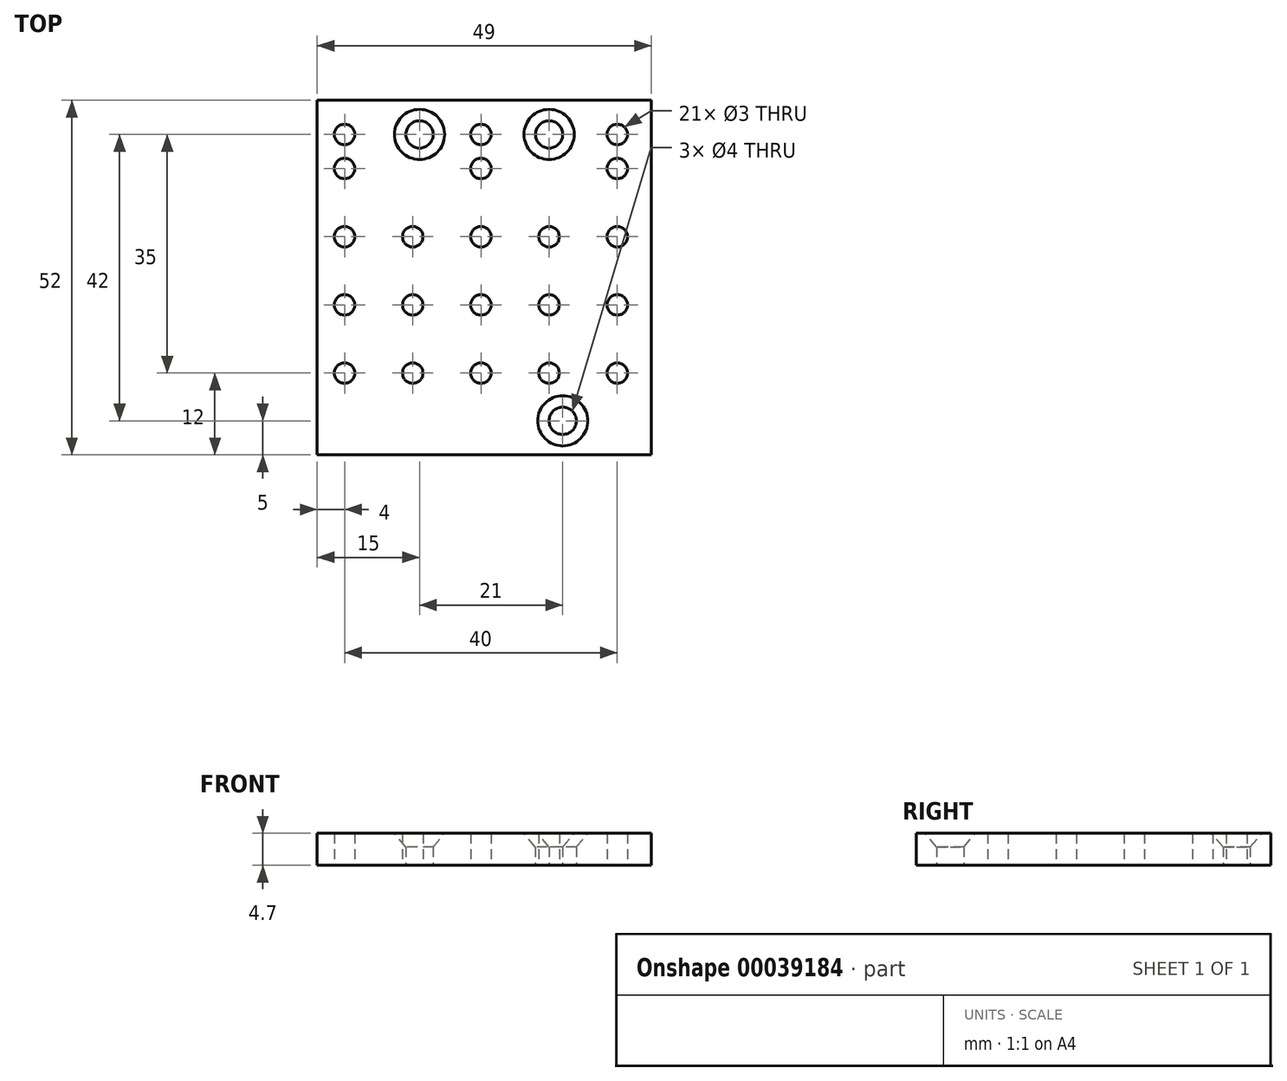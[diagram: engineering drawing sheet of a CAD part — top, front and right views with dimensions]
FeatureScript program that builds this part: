
annotation { "Feature Type Name" : "Feature", "Feature Type Description" : "" }
export const myFeature = defineFeature(function(context is Context, id is Id, definition is map)
    precondition{}
    {
        {
            var Q0;
            Q0=qCreatedBy(makeId("Top.planeOp"),FACE);
            var sketch = newSketch(context, id + "F0", { "sketchPlane" : qUnion([Q0])});
            skLineSegment(sketch, "E0", {"start": v(-52.55, 21) * mm, "end": v(60.16, 21) * mm, "construction": true});
            skLineSegment(sketch, "E1", {"start": v(-53.87, 0) * mm, "end": v(61.05, 0) * mm, "construction": true});
            skLineSegment(sketch, "E2.MirrorCS", {"start": v(-52.55, -21) * mm, "end": v(60.16, -21) * mm, "construction": true});
            skCircle(sketch, "E3", {"center": v(-28.55, 21) * mm, "radius": 2 * mm});
            skCircle(sketch, "E4", {"center": v(-9.55, 21) * mm, "radius": 2 * mm});
            skCircle(sketch, "E5", {"center": v(-7.55, -21) * mm, "radius": 2 * mm});
            skLineSegment(sketch, "E6.bottom", {"start": v(-43.55, 26) * mm, "end": v(5.45, 26) * mm});
            skLineSegment(sketch, "E6.top", {"start": v(-43.55, -26) * mm, "end": v(5.45, -26) * mm});
            skLineSegment(sketch, "E6.left", {"start": v(-43.55, 26) * mm, "end": v(-43.55, -26) * mm});
            skLineSegment(sketch, "E6.right", {"start": v(5.45, 26) * mm, "end": v(5.45, -26) * mm});
            skCircle(sketch, "E7", {"center": v(-28.55, 21) * mm, "radius": 3.5 * mm});
            skCircle(sketch, "E8", {"center": v(-9.55, 21) * mm, "radius": 3.5 * mm});
            skCircle(sketch, "E9", {"center": v(-7.55, -21) * mm, "radius": 3.5 * mm});
            skLineSegment(sketch, "E10", {"start": v(0.45, 28.16) * mm, "end": v(0.45, -29.03) * mm, "construction": true});
            skLineSegment(sketch, "E11", {"start": v(-46.97, 16) * mm, "end": v(10.41, 16) * mm, "construction": true});
            skCircle(sketch, "E12", {"center": v(-39.55, 21) * mm, "radius": 1.5 * mm});
            skCircle(sketch, "E13", {"center": v(-19.55, 21) * mm, "radius": 1.5 * mm});
            skCircle(sketch, "E14", {"center": v(0.45, 21) * mm, "radius": 1.5 * mm});
            skCircle(sketch, "E15", {"center": v(0.45, 16) * mm, "radius": 1.5 * mm});
            skCircle(sketch, "E16.0.1.0", {"center": v(0.45, 6) * mm, "radius": 1.5 * mm});
            skCircle(sketch, "E16.0.2.0", {"center": v(0.45, -4) * mm, "radius": 1.5 * mm});
            skCircle(sketch, "E16.0.3.0", {"center": v(0.45, -14) * mm, "radius": 1.5 * mm});
            skCircle(sketch, "E16.1.1.0", {"center": v(-9.55, 6) * mm, "radius": 1.5 * mm});
            skCircle(sketch, "E16.1.2.0", {"center": v(-9.55, -4) * mm, "radius": 1.5 * mm});
            skCircle(sketch, "E16.1.3.0", {"center": v(-9.55, -14) * mm, "radius": 1.5 * mm});
            skCircle(sketch, "E16.2.0.0", {"center": v(-19.55, 16) * mm, "radius": 1.5 * mm});
            skCircle(sketch, "E16.2.1.0", {"center": v(-19.55, 6) * mm, "radius": 1.5 * mm});
            skCircle(sketch, "E16.2.2.0", {"center": v(-19.55, -4) * mm, "radius": 1.5 * mm});
            skCircle(sketch, "E16.2.3.0", {"center": v(-19.55, -14) * mm, "radius": 1.5 * mm});
            skCircle(sketch, "E16.3.1.0", {"center": v(-29.55, 6) * mm, "radius": 1.5 * mm});
            skCircle(sketch, "E16.3.2.0", {"center": v(-29.55, -4) * mm, "radius": 1.5 * mm});
            skCircle(sketch, "E16.3.3.0", {"center": v(-29.55, -14) * mm, "radius": 1.5 * mm});
            skCircle(sketch, "E16.4.0.0", {"center": v(-39.55, 16) * mm, "radius": 1.5 * mm});
            skCircle(sketch, "E16.4.1.0", {"center": v(-39.55, 6) * mm, "radius": 1.5 * mm});
            skCircle(sketch, "E16.4.2.0", {"center": v(-39.55, -4) * mm, "radius": 1.5 * mm});
            skCircle(sketch, "E16.4.3.0", {"center": v(-39.55, -14) * mm, "radius": 1.5 * mm});
            skLineSegment(sketch, "E16.direction1", {"start": v(0.45, 16) * mm, "end": v(-9.55, 16) * mm, "construction": true});
            skLineSegment(sketch, "E16.direction2", {"start": v(0.45, 16) * mm, "end": v(0.45, 6) * mm, "construction": true});
            skSolve(sketch);
        }
        {
            var Q0;
            Q0=makeQuery(id+"F0.imprint","IMPRINT",FACE,{"disambiguationData":[TD([[makeQuery(id+"F0.imprint","IMPRINT",EDGE,{"derivedFrom":sQuery(id+"F0.wireOp",EDGE,"E6.bottom")}),-1.0]])]});
            var Q1;
            Q1=makeQuery(id+"F0.imprint","IMPRINT",FACE,{"disambiguationData":[TD([[makeQuery(id+"F0.imprint","IMPRINT",EDGE,{"derivedFrom":sQuery(id+"F0.wireOp",EDGE,"E3")}),-1.0]])]});
            var Q2;
            Q2=makeQuery(id+"F0.imprint","IMPRINT",FACE,{"disambiguationData":[TD([[makeQuery(id+"F0.imprint","IMPRINT",EDGE,{"derivedFrom":sQuery(id+"F0.wireOp",EDGE,"E4")}),-1.0]])]});
            var Q3;
            Q3=makeQuery(id+"F0.imprint","IMPRINT",FACE,{"disambiguationData":[TD([[makeQuery(id+"F0.imprint","IMPRINT",EDGE,{"derivedFrom":sQuery(id+"F0.wireOp",EDGE,"E5")}),-1.0]])]});
            extrude(context, id + "F1", {"entities" : qUnion([Q0, Q1, Q2, Q3]), "depth" : 4.7 * mm});
        }
        {
            var Q0;
            Q0=makeQuery(id+"F1.opExtrude","CAP_EDGE",EDGE,{"disambiguationData":[OSD([sQuery(id+"F0.wireOp",EDGE,"E3")])],"isStart":false});
            var Q1;
            Q1=makeQuery(id+"F1.opExtrude","CAP_EDGE",EDGE,{"disambiguationData":[OSD([sQuery(id+"F0.wireOp",EDGE,"E4")])],"isStart":false});
            var Q2;
            Q2=makeQuery(id+"F1.opExtrude","CAP_EDGE",EDGE,{"disambiguationData":[OSD([sQuery(id+"F0.wireOp",EDGE,"E5")])],"isStart":false});
            chamfer(context, id + "F2", {"entities" : qUnion([Q0, Q1, Q2]), "chamferType" : ChamferType.OFFSET_ANGLE, "width" : 2 * mm, "oppositeDirection" : false, "angle" : 40 * degree, "tangentPropagation" : true});
        }
    });
